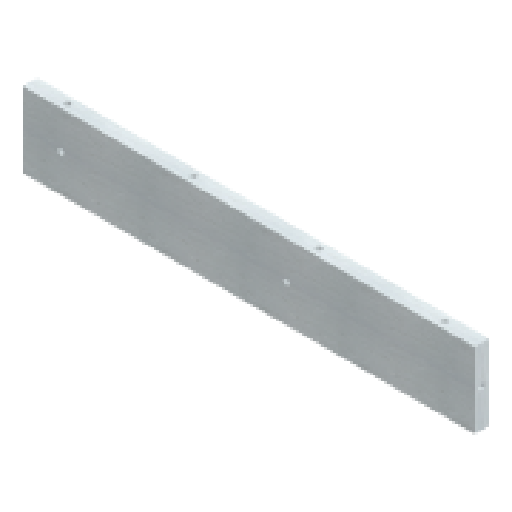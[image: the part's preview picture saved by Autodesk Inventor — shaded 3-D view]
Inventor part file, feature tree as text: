
AUTODESK INVENTOR PART (.ipt)
format: ipt  version: 2024 (Build 280153000, 153)  size: 136,192 bytes
history: native  units: in
note: dims shown in document units (in); Inventor stores cm internally (conversion verified against a paired STEP export)
features: extrude x5, sketch x5
ambient origin geometry x8: Origin, YZ Plane, XZ Plane, XY Plane, X Axis, Y Axis, Z Axis, Center Point
bodies: Solid1 (feature_tree)
feature tree (10):
  extrude  "Extrusion1"  Depth=3.937in
  extrude  "Extrusion2"  Depth=0.748in
  extrude  "Extrusion3"  Depth=0.315in
  extrude  "Extrusion4"  Depth=0.4331in TaperAngle=0.0deg
  extrude  "Extrusion5"  Depth=0.4331in
  sketch  "Sketch1"  dims[d0=23.622in d1=3.937in]
  sketch  "Sketch2"  dims[d2=0.748in d3=0.0in d4=1.9685in]
  sketch  "Sketch3"  dims[d5=9.8425in d6=0.315in]
  sketch  "Sketch4"  dims[d7=0.315in d8=0.4331in d9=0.0in]
  sketch  "Sketch5"  dims[d10=1.9685in d11=6.5617in d12=6.5617in d13=6.5617in d14=1.9685in d15=0.315in d16=0.315in d17=0.315in d18=0.315in d19=0.4331in d20=0.0in d21=0.315in d22=0.4331in d23=0.0in d24=0.315in d25=0.4331in d26=0.0in]
